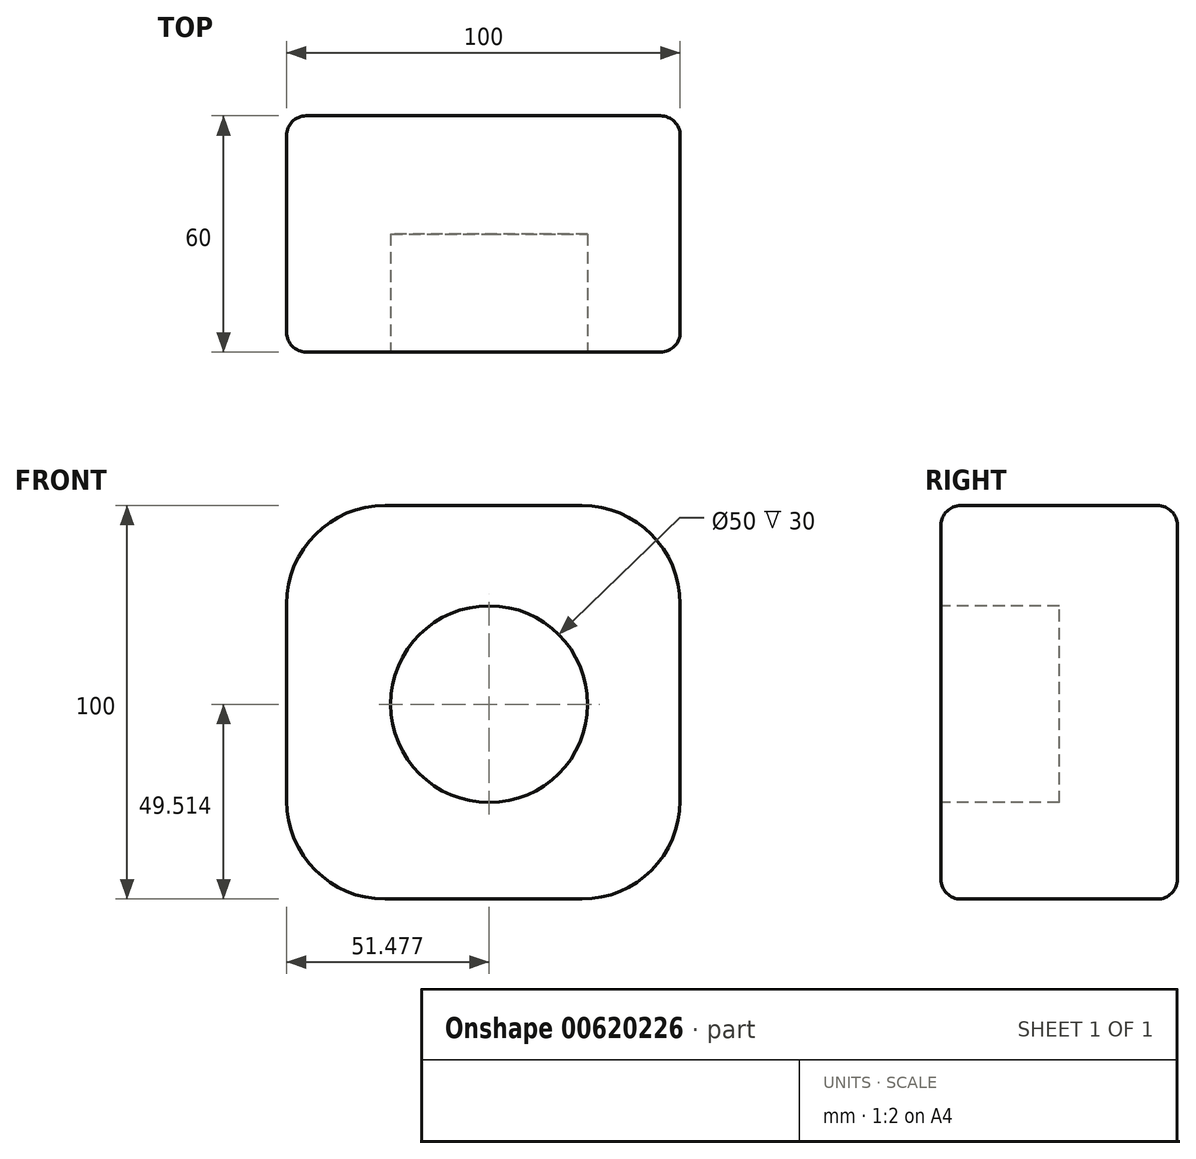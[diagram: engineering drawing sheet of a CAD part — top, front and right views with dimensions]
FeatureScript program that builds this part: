
annotation { "Feature Type Name" : "Feature", "Feature Type Description" : "" }
export const myFeature = defineFeature(function(context is Context, id is Id, definition is map)
    precondition{}
    {
        {
            var Q0;
            Q0=qCreatedBy(makeId("Front.planeOp"),FACE);
            var sketch = newSketch(context, id + "F0", { "sketchPlane" : qUnion([Q0])});
            skLineSegment(sketch, "E0.bottom", {"start": v(-21.14, 44.2) * mm, "end": v(28.86, 44.2) * mm});
            skLineSegment(sketch, "E0.top", {"start": v(-21.14, -55.8) * mm, "end": v(28.86, -55.8) * mm});
            skLineSegment(sketch, "E0.left", {"start": v(-46.14, 19.2) * mm, "end": v(-46.14, -30.8) * mm});
            skLineSegment(sketch, "E0.right", {"start": v(53.86, 19.2) * mm, "end": v(53.86, -30.8) * mm});
            skLineSegment(sketch, "E1.bottom", {"start": v(-46.14, 9.73) * mm, "end": v(-46.14, 9.73) * mm});
            skLineSegment(sketch, "E1.top", {"start": v(-46.14, 13.9) * mm, "end": v(-46.14, 13.9) * mm});
            skLineSegment(sketch, "E1.left", {"start": v(-46.14, 9.73) * mm, "end": v(-46.14, 13.9) * mm});
            skLineSegment(sketch, "E1.right", {"start": v(-46.14, 9.73) * mm, "end": v(-46.14, 13.9) * mm});
            skPoint(sketch, "E2.visualSharp", {"position": v(-46.14, 44.2) * mm});
            skArc(sketch, "E2.filletArc", {"start": v(-21.14, 44.2) * mm, "mid": v(-38.82, 36.87) * mm, "end": v(-46.14, 19.2) * mm});
            skPoint(sketch, "E3.visualSharp", {"position": v(53.86, -55.8) * mm});
            skArc(sketch, "E3.filletArc", {"start": v(28.86, -55.8) * mm, "mid": v(46.53, -48.48) * mm, "end": v(53.86, -30.8) * mm});
            skPoint(sketch, "E4.visualSharp", {"position": v(-46.14, -55.8) * mm});
            skArc(sketch, "E4.filletArc", {"start": v(-46.14, -30.8) * mm, "mid": v(-38.82, -48.48) * mm, "end": v(-21.14, -55.8) * mm});
            skPoint(sketch, "E5.visualSharp", {"position": v(53.86, 44.2) * mm});
            skArc(sketch, "E5.filletArc", {"start": v(53.86, 19.2) * mm, "mid": v(46.53, 36.87) * mm, "end": v(28.86, 44.2) * mm});
            skSolve(sketch);
        }
        {
            var Q0;
            Q0=makeQuery(id+"F0.imprint","IMPRINT",FACE,{"disambiguationData":[TD([[makeQuery(id+"F0.imprint","IMPRINT",EDGE,{"derivedFrom":sQuery(id+"F0.wireOp",EDGE,"E0.bottom")}),-1.0]])]});
            extrude(context, id + "F1", {"entities" : qUnion([Q0]), "depth" : 60 * mm, "offsetDistance" : 25 * mm});
        }
        {
            var Q0;
            Q0=makeQuery(id+"F1.opExtrude","CAP_EDGE",EDGE,{"disambiguationData":[OSD([sQuery(id+"F0.wireOp",EDGE,"E2.filletArc")])],"isStart":false});
            var Q1;
            Q1=makeQuery(id+"F1.opExtrude","CAP_FACE",FACE,{"disambiguationData":[OSD([sQuery(id+"F0.wireOp",EDGE,"E0.bottom"),sQuery(id+"F0.wireOp",EDGE,"E0.top"),sQuery(id+"F0.wireOp",EDGE,"E0.left"),sQuery(id+"F0.wireOp",EDGE,"E0.right"),sQuery(id+"F0.wireOp",EDGE,"E1.right"),sQuery(id+"F0.wireOp",EDGE,"E2.filletArc"),sQuery(id+"F0.wireOp",EDGE,"E3.filletArc"),sQuery(id+"F0.wireOp",EDGE,"E4.filletArc"),sQuery(id+"F0.wireOp",EDGE,"E5.filletArc")])],"isStart":false});
            fillet(context, id + "F2", {"entities" : qUnion([Q0, Q1]), "radius" : 5 * mm, "tangentPropagation" : true, "allowEdgeOverflow" : false});
        }
        {
            var Q0;
            Q0=makeQuery(id+"F1.opExtrude","CAP_EDGE",EDGE,{"disambiguationData":[OSD([sQuery(id+"F0.wireOp",EDGE,"E0.right")])],"isStart":true});
            var Q1;
            Q1=makeQuery(id+"F1.opExtrude","CAP_FACE",FACE,{"disambiguationData":[OSD([sQuery(id+"F0.wireOp",EDGE,"E0.bottom"),sQuery(id+"F0.wireOp",EDGE,"E0.top"),sQuery(id+"F0.wireOp",EDGE,"E0.left"),sQuery(id+"F0.wireOp",EDGE,"E0.right"),sQuery(id+"F0.wireOp",EDGE,"E1.right"),sQuery(id+"F0.wireOp",EDGE,"E2.filletArc"),sQuery(id+"F0.wireOp",EDGE,"E3.filletArc"),sQuery(id+"F0.wireOp",EDGE,"E4.filletArc"),sQuery(id+"F0.wireOp",EDGE,"E5.filletArc")])],"isStart":true});
            fillet(context, id + "F3", {"entities" : qUnion([Q0, Q1]), "radius" : 5 * mm, "tangentPropagation" : true, "allowEdgeOverflow" : false});
        }
        {
            var Q0;
            Q0=makeQuery(id+"F1.opExtrude","CAP_FACE",FACE,{"disambiguationData":[OSD([sQuery(id+"F0.wireOp",EDGE,"E0.bottom"),sQuery(id+"F0.wireOp",EDGE,"E0.top"),sQuery(id+"F0.wireOp",EDGE,"E0.left"),sQuery(id+"F0.wireOp",EDGE,"E0.right"),sQuery(id+"F0.wireOp",EDGE,"E1.right"),sQuery(id+"F0.wireOp",EDGE,"E2.filletArc"),sQuery(id+"F0.wireOp",EDGE,"E3.filletArc"),sQuery(id+"F0.wireOp",EDGE,"E4.filletArc"),sQuery(id+"F0.wireOp",EDGE,"E5.filletArc")])],"isStart":false});
            var sketch = newSketch(context, id + "F4", { "sketchPlane" : qUnion([Q0])});
            skSolve(sketch);
        }
        {
            var Q0;
            Q0=qCreatedBy(makeId("Front.planeOp"),FACE);
            var sketch = newSketch(context, id + "F5", { "sketchPlane" : qUnion([Q0])});
            skCircle(sketch, "E6", {"center": v(0, 0) * mm, "radius": 25 * mm});
            skSolve(sketch);
        }
        {
            var Q0;
            Q0=makeQuery(id+"F5.imprint","IMPRINT",FACE,{"disambiguationData":[TD([[makeQuery(id+"F5.imprint","IMPRINT",EDGE,{"derivedFrom":sQuery(id+"F5.wireOp",EDGE,"E6")}),1.0]])]});
            extrude(context, id + "F6", {"entities" : qUnion([Q0]), "operationType" : NewBodyOperationType.REMOVE, "oppositeDirection" : true, "depth" : 30 * mm, "offsetDistance" : 25 * mm});
        }
        {
            var Q0;
            {var subQ0=sQuery(id+"F0.wireOp",EDGE,"E5.filletArc");var subQ1=sQuery(id+"F0.wireOp",EDGE,"E4.filletArc");var subQ2=sQuery(id+"F0.wireOp",EDGE,"E3.filletArc");var subQ3=sQuery(id+"F0.wireOp",EDGE,"E2.filletArc");var subQ4=sQuery(id+"F0.wireOp",EDGE,"E1.right");var subQ5=sQuery(id+"F0.wireOp",EDGE,"E0.right");var subQ6=sQuery(id+"F0.wireOp",EDGE,"E0.left");var subQ7=sQuery(id+"F0.wireOp",EDGE,"E0.top");var subQ8=sQuery(id+"F0.wireOp",EDGE,"E0.bottom");var subQ9=makeQuery(id+"F1.opExtrude","CAP_FACE",FACE,{"disambiguationData":[OSD([subQ8,subQ7,subQ6,subQ5,subQ4,subQ3,subQ2,subQ1,subQ0])],"isStart":false});Q0=makeQuery(id+"F4.imprint","IMPRINT",FACE,{"disambiguationData":[TD([[makeQuery(id+"F4.imprint","IMPRINT",EDGE,{"derivedFrom":makeQuery(id+"F2.opFillet","BLEND_EDGE",EDGE,{"blendedFrom":[makeQuery(id+"F1.opExtrude","CAP_EDGE",EDGE,{"disambiguationData":[OSD([subQ8])],"isStart":false}),subQ9],"blendedInto":[subQ9]})}),1.0]])]});}
            var sketch = newSketch(context, id + "F7", { "sketchPlane" : qUnion([Q0])});
            skCircle(sketch, "E7", {"center": v(5.34, -6.29) * mm, "radius": 25 * mm});
            skSolve(sketch);
        }
        {
            var Q0;
            Q0 = qSketchRegion(id + "F7", true);
            extrude(context, id + "F8", {"entities" : qUnion([Q0]), "operationType" : NewBodyOperationType.REMOVE, "oppositeDirection" : true, "depth" : 30 * mm, "offsetDistance" : 25 * mm});
        }
    });
